# Revit family: EKF_EE_ДверьПрозрачнаяTrivia_AVERES
name_source: partatom
category: Электрооборудование
units: mm (PartAtom-declared; Revit-internal decimal feet)

## family parameters
Всегда вертикально = Нет
На основе рабочей плоскости = Да
Общий = Да
При загрузке вырезать с полостями = Нет
Размер круглого соединителя = Использовать диаметр
Тип детали = Силовой щит
Точка расчета площади = Нет

## types (3) — shared parameters
ADSK_Единица измерения = шт.
ADSK_Завод-изготовитель = EKF
ADSK_Количество = 1
ADSK_Марка = Дверь прозрачная
ADSK_Материал = RAL 7035_Сталь
ADSK_Обозначение = Дверь прозрачная
ADSK_Размер_Высота = 2013 мм
ADSK_Размер_Глубина = 30 мм
Изготовитель = EKF
Карман для документации = Да
КолОтв = 4
Отметка по умолчанию = 1219.2 мм
Серия номенклатуры = Averes
ТВ = EKF_2_TRIVIA_AVERES
Тип установки = -
ТипДверцы = Вл_ДверцаПрозрачная
zero-valued in all types: ADSK_Масса

## per-type parameters (varying)
| type | ADSK_Код изделия | ADSK_Размер_Ширина | Степень защиты IP | Тип |
| Дверь прозрачная Ш600 IP55 EKF AVERES | D2G600WP | 600 мм | IP55 | 416 мм |
| Дверь прозрачная Ш800 IP30 EKF AVERES | D2G800 | 800 мм | IP30 | 417 мм |
| Дверь прозрачная Ш800 IP55 EKF AVERES | D2G800WP | 800 мм | IP55 | 418 мм |

note: column(s) folded — value = type name in every type: ADSK_Наименование
